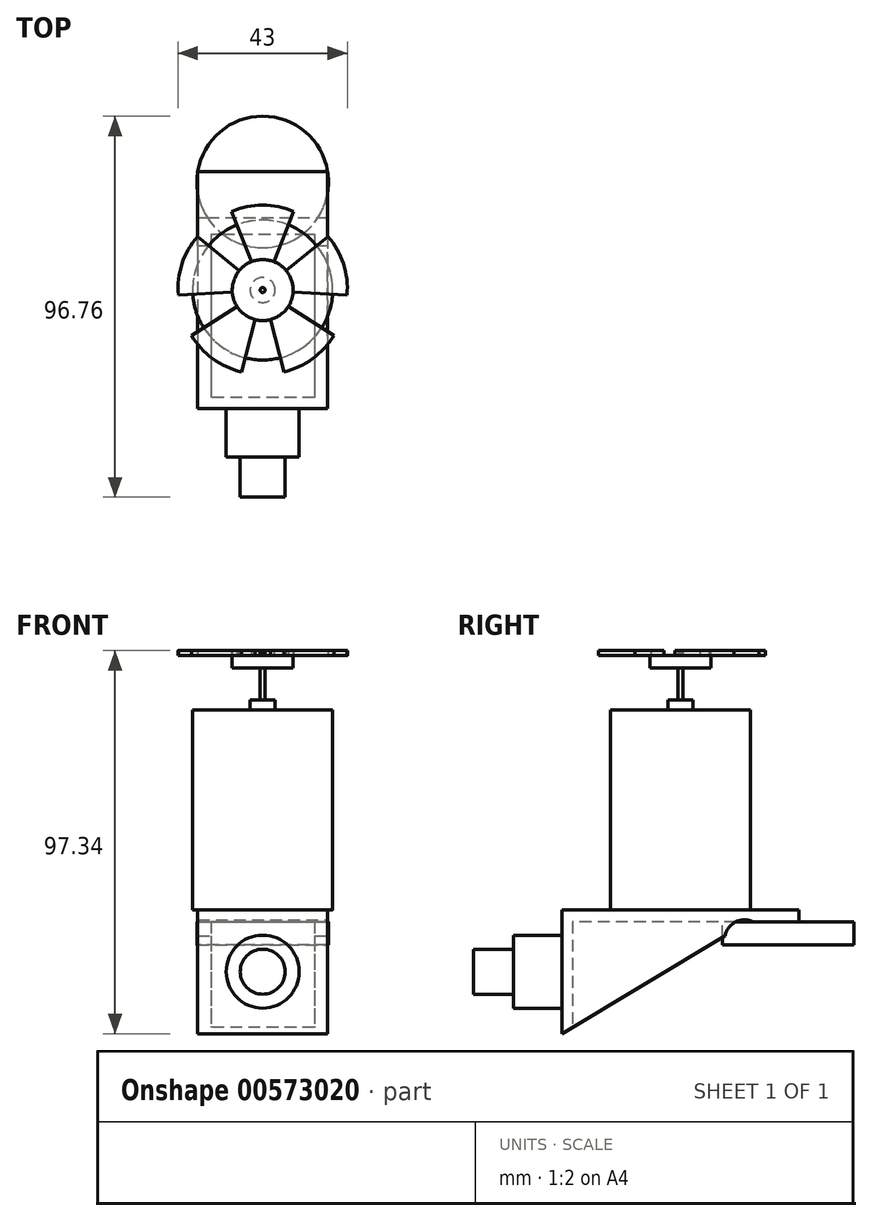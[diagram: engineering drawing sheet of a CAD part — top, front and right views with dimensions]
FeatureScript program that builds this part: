
annotation { "Feature Type Name" : "Feature", "Feature Type Description" : "" }
export const myFeature = defineFeature(function(context is Context, id is Id, definition is map)
    precondition{}
    {
        {
            var Q0;
            Q0=qCreatedBy(makeId("Top.planeOp"),FACE);
            var sketch = newSketch(context, id + "F0", { "sketchPlane" : qUnion([Q0])});
            skLineSegment(sketch, "E0", {"start": v(0, 0) * mm, "end": v(0, 35.56) * mm});
            skCircle(sketch, "E1", {"center": v(0, 17.78) * mm, "radius": 17.78 * mm});
            skSolve(sketch);
        }
        {
            var Q0;
            {var subQ0=sQuery(id+"F0.wireOp",EDGE,"E0");Q0=makeQuery(id+"F0.imprint","IMPRINT",FACE,{"disambiguationData":[TD([[makeQuery(id+"F0.imprint","IMPRINT",EDGE,{"derivedFrom":subQ0}),-1.0]])]});}
            var Q1;
            {var subQ0=sQuery(id+"F0.wireOp",EDGE,"E0");Q1=makeQuery(id+"F0.imprint","IMPRINT",FACE,{"disambiguationData":[TD([[makeQuery(id+"F0.imprint","IMPRINT",EDGE,{"derivedFrom":subQ0}),1.0]])]});}
            extrude(context, id + "F1", {"entities" : qUnion([Q0, Q1]), "depth" : 50.8 * mm, "offsetDistance" : 25.4 * mm});
        }
        {
            var Q0;
            Q0=makeQuery(id+"F1.opExtrude","CAP_FACE",FACE,{"disambiguationData":[OSD([sQuery(id+"F0.wireOp",EDGE,"E1")])],"isStart":false});
            var sketch = newSketch(context, id + "F2", { "sketchPlane" : qUnion([Q0])});
            skCircle(sketch, "E2", {"center": v(0, 17.78) * mm, "radius": 3.17 * mm});
            skSolve(sketch);
        }
        {
            var Q0;
            Q0 = qSketchRegion(id + "F2", true);
            var Q1;
            Q1=makeQuery(id+"F2.imprint","IMPRINT",FACE,{"disambiguationData":[TD([[makeQuery(id+"F2.imprint","IMPRINT",EDGE,{"derivedFrom":sQuery(id+"F2.wireOp",EDGE,"E2")}),1.0]])]});
            extrude(context, id + "F3", {"entities" : qUnion([Q0, Q1]), "operationType" : NewBodyOperationType.ADD, "depth" : 2.54 * mm, "offsetDistance" : 25.4 * mm});
        }
        {
            var Q0;
            Q0=makeQuery(id+"F3.opExtrude","CAP_FACE",FACE,{"disambiguationData":[OSD([sQuery(id+"F2.wireOp",EDGE,"E2")])],"isStart":false});
            var sketch = newSketch(context, id + "F4", { "sketchPlane" : qUnion([Q0])});
            skCircle(sketch, "E3", {"center": v(0, 17.78) * mm, "radius": 0.64 * mm});
            skSolve(sketch);
        }
        {
            var Q0;
            Q0=makeQuery(id+"F4.imprint","IMPRINT",FACE,{"disambiguationData":[TD([[makeQuery(id+"F4.imprint","IMPRINT",EDGE,{"derivedFrom":sQuery(id+"F4.wireOp",EDGE,"E3")}),1.0]])]});
            extrude(context, id + "F5", {"entities" : qUnion([Q0]), "operationType" : NewBodyOperationType.ADD, "depth" : 8.05 * mm, "offsetDistance" : 25.4 * mm});
        }
        {
            var Q0;
            Q0=makeQuery(id+"F5.opExtrude","CAP_FACE",FACE,{"disambiguationData":[OSD([sQuery(id+"F4.wireOp",EDGE,"E3")])],"isStart":false});
            var sketch = newSketch(context, id + "F6", { "sketchPlane" : qUnion([Q0])});
            skCircle(sketch, "E4", {"center": v(0, 17.78) * mm, "radius": 7.76 * mm});
            skSolve(sketch);
        }
        {
            var Q0;
            Q0 = qSketchRegion(id + "F6", true);
            extrude(context, id + "F7", {"entities" : qUnion([Q0]), "operationType" : NewBodyOperationType.ADD, "depth" : 3.17 * mm, "offsetDistance" : 25.4 * mm});
        }
        {
            var Q0;
            Q0=makeQuery(id+"F7.opExtrude","CAP_FACE",FACE,{"disambiguationData":[OSD([sQuery(id+"F6.wireOp",EDGE,"E4")])],"isStart":false});
            var sketch = newSketch(context, id + "F8", { "sketchPlane" : qUnion([Q0])});
            skLineSegment(sketch, "E5", {"start": v(-2.84, 25) * mm, "end": v(-7.86, 37.75) * mm});
            skLineSegment(sketch, "E6", {"start": v(0, 25.5) * mm, "end": v(0, 43.82) * mm, "construction": true});
            skLineSegment(sketch, "E7.MirrorCS", {"start": v(2.84, 25) * mm, "end": v(7.86, 37.75) * mm});
            skArc(sketch, "E8", {"start": v(7.86, 37.75) * mm, "mid": v(0, 39.35) * mm, "end": v(-7.86, 37.75) * mm});
            skArc(sketch, "E9", {"start": v(2.84, 25) * mm, "mid": v(0, 25.5) * mm, "end": v(-2.84, 25) * mm});
            skLineSegment(sketch, "E10.1.0", {"start": v(-5.99, 22.71) * mm, "end": v(-16.57, 31.42) * mm});
            skLineSegment(sketch, "E10.1.1", {"start": v(-7.75, 17.31) * mm, "end": v(-21.42, 16.48) * mm});
            skArc(sketch, "E10.1.2", {"start": v(-16.57, 31.42) * mm, "mid": v(-20.51, 24.45) * mm, "end": v(-21.42, 16.48) * mm});
            skArc(sketch, "E10.1.3", {"start": v(-5.99, 22.71) * mm, "mid": v(-7.33, 20.16) * mm, "end": v(-7.75, 17.31) * mm});
            skLineSegment(sketch, "E10.2.0", {"start": v(-6.54, 13.6) * mm, "end": v(-18.1, 6.24) * mm});
            skLineSegment(sketch, "E10.2.1", {"start": v(-1.95, 10.27) * mm, "end": v(-5.38, -3) * mm});
            skArc(sketch, "E10.2.2", {"start": v(-18.1, 6.24) * mm, "mid": v(-12.68, 0.33) * mm, "end": v(-5.38, -3) * mm});
            skArc(sketch, "E10.2.3", {"start": v(-6.54, 13.6) * mm, "mid": v(-4.53, 11.54) * mm, "end": v(-1.95, 10.27) * mm});
            skLineSegment(sketch, "E10.3.0", {"start": v(1.95, 10.27) * mm, "end": v(5.38, -3) * mm});
            skLineSegment(sketch, "E10.3.1", {"start": v(6.54, 13.6) * mm, "end": v(18.1, 6.24) * mm});
            skArc(sketch, "E10.3.2", {"start": v(5.38, -3) * mm, "mid": v(12.68, 0.33) * mm, "end": v(18.1, 6.24) * mm});
            skArc(sketch, "E10.3.3", {"start": v(1.95, 10.27) * mm, "mid": v(4.53, 11.54) * mm, "end": v(6.54, 13.6) * mm});
            skLineSegment(sketch, "E10.4.0", {"start": v(7.75, 17.31) * mm, "end": v(21.42, 16.48) * mm});
            skLineSegment(sketch, "E10.4.1", {"start": v(5.99, 22.71) * mm, "end": v(16.57, 31.42) * mm});
            skArc(sketch, "E10.4.2", {"start": v(21.42, 16.48) * mm, "mid": v(20.51, 24.45) * mm, "end": v(16.57, 31.42) * mm});
            skArc(sketch, "E10.4.3", {"start": v(7.75, 17.31) * mm, "mid": v(7.33, 20.16) * mm, "end": v(5.99, 22.71) * mm});
            skPoint(sketch, "E10.center", {"position": v(0, 17.78) * mm});
            skSolve(sketch);
        }
        {
            var Q0;
            Q0 = qSketchRegion(id + "F8", true);
            extrude(context, id + "F9", {"entities" : qUnion([Q0]), "operationType" : NewBodyOperationType.ADD, "depth" : 1.27 * mm, "offsetDistance" : 25.4 * mm});
        }
        {
            var Q0;
            Q0=makeQuery(id+"F7.opExtrude","CAP_FACE",FACE,{"disambiguationData":[OSD([sQuery(id+"F6.wireOp",EDGE,"E4")])],"isStart":false});
            extrude(context, id + "F10", {"entities" : qUnion([Q0]), "operationType" : NewBodyOperationType.ADD, "depth" : 0.25 / 50.8 * mm, "offsetDistance" : 25.4 * mm});
        }
        {
            var Q0;
            Q0=makeQuery(id+"F10.opExtrude","CAP_FACE",FACE,{"disambiguationData":[OSD([sQuery(id+"F6.wireOp",EDGE,"E4")])],"isStart":false});
            var sketch = newSketch(context, id + "F11", { "sketchPlane" : qUnion([Q0])});
            skCircle(sketch, "E11", {"center": v(0, 17.78) * mm, "radius": 0.64 * mm});
            skSolve(sketch);
        }
        {
            var Q0;
            Q0 = qSketchRegion(id + "F11", true);
            extrude(context, id + "F12", {"entities" : qUnion([Q0]), "operationType" : NewBodyOperationType.ADD, "depth" : 0.84 * mm, "offsetDistance" : 25.4 * mm});
        }
        {
            var Q0;
            Q0=makeQuery(id+"F1.opExtrude","CAP_FACE",FACE,{"disambiguationData":[OSD([sQuery(id+"F0.wireOp",EDGE,"E1")])],"isStart":true});
            var sketch = newSketch(context, id + "F13", { "sketchPlane" : qUnion([Q0])});
            skLineSegment(sketch, "E12", {"start": v(-16.51, -17.78) * mm, "end": v(-16.51, 12.32) * mm});
            skLineSegment(sketch, "E13.MirrorCS", {"start": v(-16.51, -17.78) * mm, "end": v(-16.51, -47.88) * mm});
            skLineSegment(sketch, "E14.MirrorCS", {"start": v(16.51, -17.78) * mm, "end": v(16.51, 12.32) * mm});
            skLineSegment(sketch, "E15.MirrorCS", {"start": v(16.51, -17.78) * mm, "end": v(16.51, -47.88) * mm});
            skLineSegment(sketch, "E16", {"start": v(-16.51, 12.32) * mm, "end": v(16.51, 12.32) * mm});
            skLineSegment(sketch, "E17", {"start": v(-16.51, -47.88) * mm, "end": v(16.51, -47.88) * mm});
            skPoint(sketch, "E18.start.orphan", {"position": v(0, -17.78) * mm});
            skSolve(sketch);
        }
        {
            var Q0;
            {var subQ0=sQuery(id+"F13.wireOp",EDGE,"E16");Q0=makeQuery(id+"F13.imprint","IMPRINT",FACE,{"disambiguationData":[TD([[makeQuery(id+"F13.imprint","IMPRINT",EDGE,{"derivedFrom":subQ0}),-1.0]])]});}
            var Q1;
            {var subQ0=sQuery(id+"F13.wireOp",EDGE,"E17");Q1=makeQuery(id+"F13.imprint","IMPRINT",FACE,{"disambiguationData":[TD([[makeQuery(id+"F13.imprint","IMPRINT",EDGE,{"derivedFrom":subQ0}),1.0]])]});}
            var Q2;
            {var subQ6=sQuery(id+"F13.wireOp",EDGE,"E13.MirrorCS");var subQ7=sQuery(id+"F13.wireOp",EDGE,"E12");var subQ8=makeQuery(id+"F13.imprint","INTERSECT",VERTEX,{"derivedFrom":[subQ7,subQ6]});Q2=makeQuery(id+"F13.imprint","IMPRINT",FACE,{"disambiguationData":[TD([[makeQuery(id+"F13.imprint","IMPRINT",EDGE,{"disambiguationData":[TD([[subQ8,-1.0]])],"derivedFrom":subQ7}),-1.0]])]});}
            extrude(context, id + "F14", {"entities" : qUnion([Q0, Q1, Q2]), "operationType" : NewBodyOperationType.ADD, "depth" : 31.5 * mm, "offsetDistance" : 25.4 * mm});
        }
        {
            var Q0;
            Q0=makeQuery(id+"F14.opExtrude","SWEPT_FACE",FACE,{"disambiguationData":[OSD([sQuery(id+"F13.wireOp",EDGE,"E14.MirrorCS"),sQuery(id+"F13.wireOp",EDGE,"E15.MirrorCS")])]});
            var sketch = newSketch(context, id + "F15", { "sketchPlane" : qUnion([Q0])});
            skLineSegment(sketch, "E19", {"start": v(-12.32, -31.5) * mm, "end": v(29.14, -6.65) * mm});
            skLineSegment(sketch, "E20", {"start": v(47.88, -3.05) * mm, "end": v(36.23, -3.05) * mm});
            skArc(sketch, "E21", {"start": v(36.23, -3.05) * mm, "mid": v(31.81, -3.15) * mm, "end": v(29.14, -6.65) * mm});
            skLineSegment(sketch, "E22", {"start": v(-12.32, -31.5) * mm, "end": v(47.88, -31.5) * mm});
            skLineSegment(sketch, "E23", {"start": v(47.88, -3.05) * mm, "end": v(47.88, -31.5) * mm});
            skSolve(sketch);
        }
        {
            var Q0;
            Q0 = qSketchRegion(id + "F15", true);
            extrude(context, id + "F16", {"entities" : qUnion([Q0]), "operationType" : NewBodyOperationType.REMOVE, "oppositeDirection" : true, "depth" : 51.82 * mm, "offsetDistance" : 25.4 * mm});
        }
        {
            var Q0;
            Q0=qCreatedBy(makeId("Top.planeOp"),FACE);
            cPlane(context, id + "F17", {"entities" : qUnion([Q0]), "cplaneType" : CPlaneType.OFFSET, "offset" : 31.5 * mm, "oppositeDirection" : true, "width" : 152.4 * mm, "height" : 152.4 * mm});
        }
        {
            var Q0;
            Q0=qCreatedBy(id+"F17.planeOp",FACE);
            var sketch = newSketch(context, id + "F18", { "sketchPlane" : qUnion([Q0])});
            skLineSegment(sketch, "E24.bottom", {"start": v(13.17, 45.07) * mm, "end": v(-13.17, 45.07) * mm});
            skLineSegment(sketch, "E24.top", {"start": v(13.17, -9.56) * mm, "end": v(-13.17, -9.56) * mm});
            skLineSegment(sketch, "E24.left", {"start": v(13.17, 45.07) * mm, "end": v(13.17, -9.56) * mm});
            skLineSegment(sketch, "E24.right", {"start": v(-13.17, 45.07) * mm, "end": v(-13.17, -9.56) * mm});
            skPoint(sketch, "E24.middle", {"position": v(0, 17.75) * mm});
            skSolve(sketch);
        }
        {
            var Q0;
            Q0=makeQuery(id+"F18.imprint","IMPRINT",FACE,{"disambiguationData":[TD([[makeQuery(id+"F18.imprint","IMPRINT",EDGE,{"derivedFrom":sQuery(id+"F18.wireOp",EDGE,"E24.bottom")}),1.0]])]});
            extrude(context, id + "F19", {"entities" : qUnion([Q0]), "operationType" : NewBodyOperationType.REMOVE, "depth" : 28.45 * mm, "offsetDistance" : 25.4 * mm});
        }
        {
            var Q0;
            Q0=makeQuery(id+"F16.boolean.opBoolean","COPY",FACE,{"derivedFrom":makeQuery(id+"F16.opExtrude","SWEPT_FACE",FACE,{"disambiguationData":[OSD([sQuery(id+"F15.wireOp",EDGE,"E20")])]})});
            var sketch = newSketch(context, id + "F20", { "sketchPlane" : qUnion([Q0])});
            skLineSegment(sketch, "E25", {"start": v(0, -61.98) * mm, "end": v(7.38, -61.98) * mm});
            skLineSegment(sketch, "E26", {"start": v(0, -61.98) * mm, "end": v(0, -31.97) * mm});
            skPoint(sketch, "E26.endSnap0", {"position": v(0, -36.23) * mm});
            skCircle(sketch, "E27", {"center": v(0, -45.25) * mm, "radius": 16.7 * mm});
            skSolve(sketch);
        }
        {
            var Q0;
            Q0 = qSketchRegion(id + "F20", true);
            extrude(context, id + "F21", {"entities" : qUnion([Q0]), "operationType" : NewBodyOperationType.ADD, "depth" : 5.94 * mm, "offsetDistance" : 25.4 * mm});
        }
        {
            var Q0;
            Q0=makeQuery(id+"F14.opExtrude","SWEPT_FACE",FACE,{"disambiguationData":[OSD([sQuery(id+"F13.wireOp",EDGE,"E16")])]});
            var sketch = newSketch(context, id + "F22", { "sketchPlane" : qUnion([Q0])});
            skCircle(sketch, "E28", {"center": v(0, -15.75) * mm, "radius": 9.27 * mm});
            skSolve(sketch);
        }
        {
            var Q0;
            Q0=makeQuery(id+"F22.imprint","IMPRINT",FACE,{"disambiguationData":[TD([[makeQuery(id+"F22.imprint","IMPRINT",EDGE,{"derivedFrom":sQuery(id+"F22.wireOp",EDGE,"E28")}),1.0]])]});
            extrude(context, id + "F23", {"entities" : qUnion([Q0]), "operationType" : NewBodyOperationType.ADD, "depth" : 12.33 * mm, "offsetDistance" : 25.4 * mm});
        }
        {
            var Q0;
            Q0=qCreatedBy(makeId("Right.planeOp"),FACE);
            var sketch = newSketch(context, id + "F24", { "sketchPlane" : qUnion([Q0])});
            skCircle(sketch, "E29", {"center": v(-18.51, -15.42) * mm, "radius": 4.01 * mm});
            skSolve(sketch);
        }
        {
            var Q0;
            Q0=makeQuery(id+"FGzurXzU5Xh1jvE_1.opExtrude","CAP_FACE",FACE,{"disambiguationData":[OSD([sQuery(id+"F24.wireOp",EDGE,"E29")])],"isStart":false});
            var sketch = newSketch(context, id + "F25", { "sketchPlane" : qUnion([Q0])});
            skCircle(sketch, "E30", {"center": v(-18.51, -15.42) * mm, "radius": 5.72 * mm});
            skSolve(sketch);
        }
        {
            var Q0;
            Q0=makeQuery(id+"F23.opExtrude","CAP_FACE",FACE,{"disambiguationData":[OSD([sQuery(id+"F22.wireOp",EDGE,"E28")])],"isStart":false});
            var sketch = newSketch(context, id + "F26", { "sketchPlane" : qUnion([Q0])});
            skCircle(sketch, "E31", {"center": v(0, -15.75) * mm, "radius": 5.72 * mm});
            skSolve(sketch);
        }
        {
            var Q0;
            Q0 = qSketchRegion(id + "F26", true);
            extrude(context, id + "F27", {"entities" : qUnion([Q0]), "operationType" : NewBodyOperationType.ADD, "depth" : 10.16 * mm, "offsetDistance" : 25.4 * mm});
        }
    });
